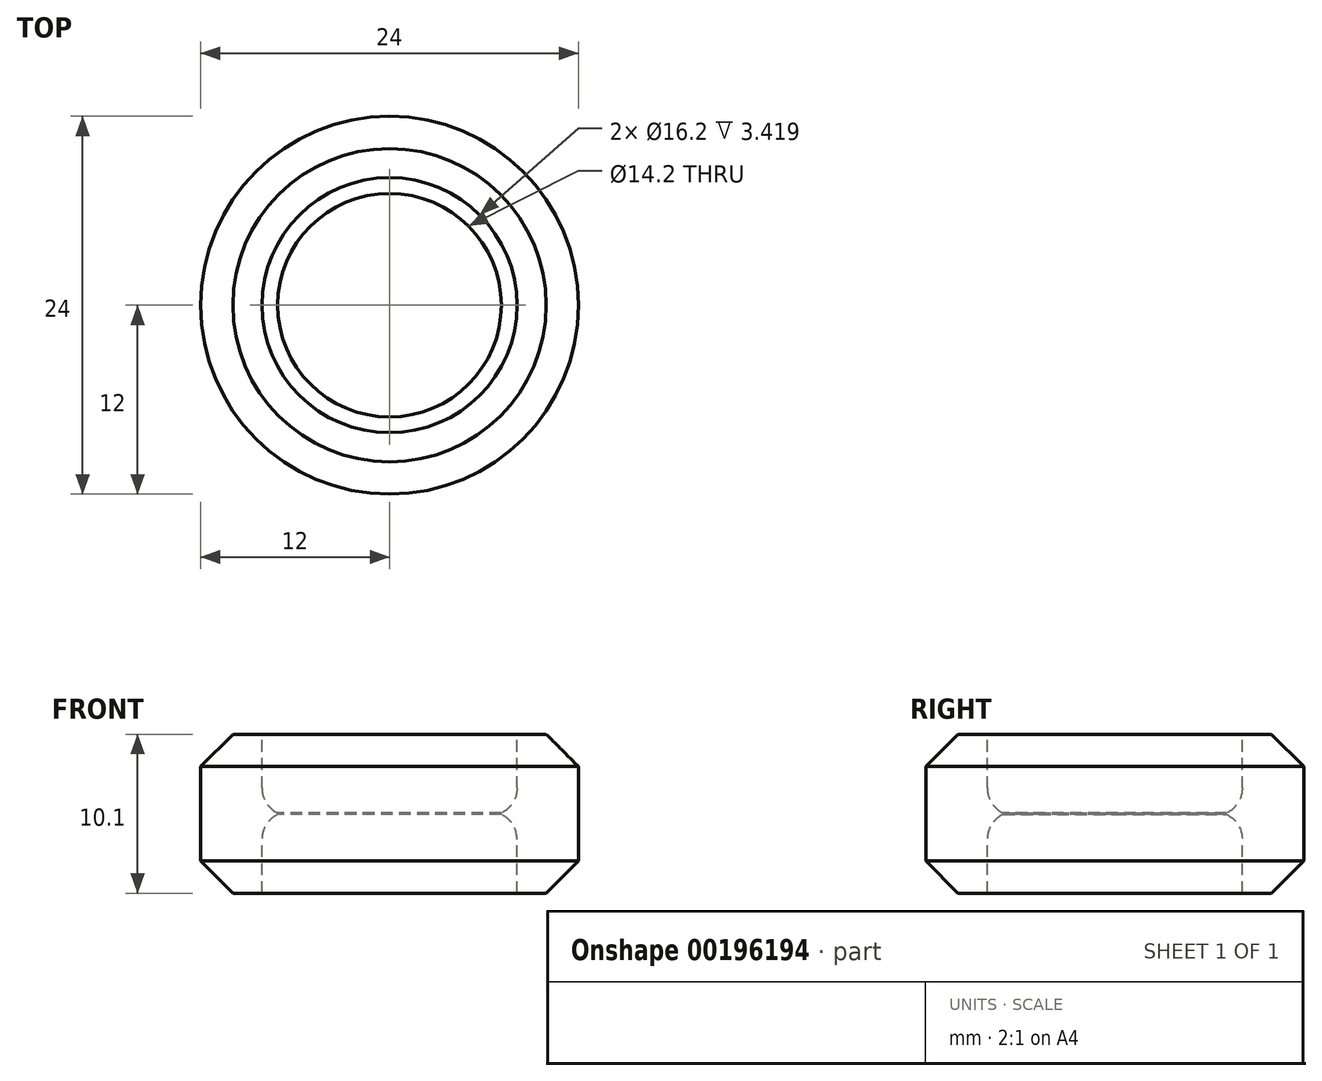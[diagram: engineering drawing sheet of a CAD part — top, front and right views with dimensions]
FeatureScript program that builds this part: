
annotation { "Feature Type Name" : "Feature", "Feature Type Description" : "" }
export const myFeature = defineFeature(function(context is Context, id is Id, definition is map)
    precondition{}
    {
        {
            var Q0;
            Q0=qCreatedBy(makeId("Front.planeOp"),FACE);
            var sketch = newSketch(context, id + "F0", { "sketchPlane" : qUnion([Q0])});
            skLineSegment(sketch, "E0", {"start": v(0, 0) * mm, "end": v(-5.09, 0) * mm, "construction": true});
            skPoint(sketch, "E1", {"position": v(-5.09, 0) * mm});
            skLineSegment(sketch, "E2", {"start": v(-8.1, 0.05) * mm, "end": v(-8.1, 5.05) * mm});
            skLineSegment(sketch, "E3.MirrorCS", {"start": v(-8.1, -0.05) * mm, "end": v(-8.1, -5.05) * mm});
            skLineSegment(sketch, "E4", {"start": v(-12, -3) * mm, "end": v(-12, 3) * mm});
            skPoint(sketch, "E5", {"position": v(-12, 0) * mm});
            skLineSegment(sketch, "E6", {"start": v(-12, -3) * mm, "end": v(-9.95, -5.05) * mm});
            skLineSegment(sketch, "E7", {"start": v(-8.1, -5.05) * mm, "end": v(-9.95, -5.05) * mm});
            skLineSegment(sketch, "E8.MirrorCS", {"start": v(-12, 3) * mm, "end": v(-9.95, 5.05) * mm});
            skLineSegment(sketch, "E9.MirrorCS", {"start": v(-8.1, 5.05) * mm, "end": v(-9.95, 5.05) * mm});
            skLineSegment(sketch, "E10", {"start": v(0, 21.82) * mm, "end": v(0, 0) * mm, "construction": true});
            skLineSegment(sketch, "E11", {"start": v(-8.1, 0.05) * mm, "end": v(-7.1, 0.05) * mm});
            skLineSegment(sketch, "E12.MirrorCS", {"start": v(-8.1, -0.05) * mm, "end": v(-7.1, -0.05) * mm});
            skLineSegment(sketch, "E13", {"start": v(-7.1, 0.05) * mm, "end": v(-7.1, -0.05) * mm});
            skSolve(sketch);
        }
        {
            var Q0;
            Q0=makeQuery(id+"F0.imprint","IMPRINT",FACE,{"disambiguationData":[TD([[makeQuery(id+"F0.imprint","IMPRINT",EDGE,{"derivedFrom":sQuery(id+"F0.wireOp",EDGE,"E2")}),1.0]])]});
            var Q1;
            Q1=sQuery(id+"F0.wireOp",EDGE,"E10");
            revolve(context, id + "F1", {"entities" : qUnion([Q0]), "axis" : qUnion([Q1]), "revolveType" : RevolveType.FULL});
        }
        {
            var Q0;
            Q0=makeQuery(id+"F1.opRevolve","SWEPT_EDGE",EDGE,{"disambiguationData":[OSD([sQuery(id+"F0.wireOp",EDGE,"E3.MirrorCS"),sQuery(id+"F0.wireOp",EDGE,"E12.MirrorCS")])]});
            var Q1;
            Q1=makeQuery(id+"F1.opRevolve","SWEPT_EDGE",EDGE,{"disambiguationData":[OSD([sQuery(id+"F0.wireOp",EDGE,"E2"),sQuery(id+"F0.wireOp",EDGE,"E11")])]});
            fillet(context, id + "F2", {"entities" : qUnion([Q0, Q1]), "radius" : 1.75 * mm, "tangentPropagation" : true, "allowEdgeOverflow" : false});
        }
    });
